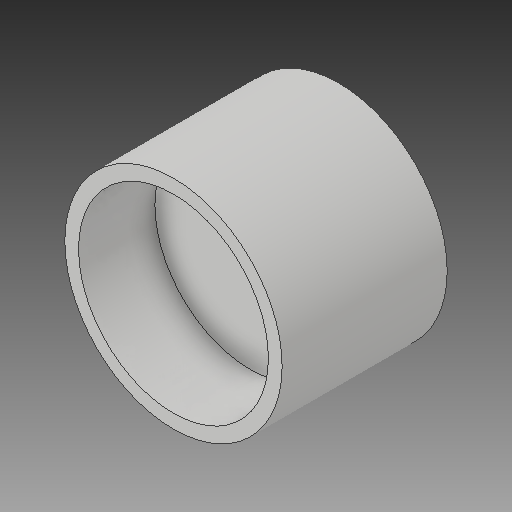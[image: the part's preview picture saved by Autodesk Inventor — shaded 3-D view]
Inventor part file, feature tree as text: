
AUTODESK INVENTOR PART (.ipt)
format: ipt  version: 2019 (Build 230136000, 136)  size: 157,184 bytes
history: native  units: in
note: dims shown in document units (in); Inventor stores cm internally (conversion verified against a paired STEP export)
features: sketch x5, other x3
ambient origin geometry x8: Origin, YZ Plane, XZ Plane, XY Plane, X Axis, Y Axis, Z Axis, Center Point
bodies: Solid1 (feature_tree)
feature tree (8):
  other  "Wheel_Rim.ipt"
  other  "Solid1::Wheel_Rim.ipt"
  other  "TaggingFeature1"
  sketch  "Sketch1"  dims[d0=0.3937in]
  sketch  "Sketch2"
  sketch  "Sketch3"
  sketch  "Sketch4"
  sketch  "Sketch5"
